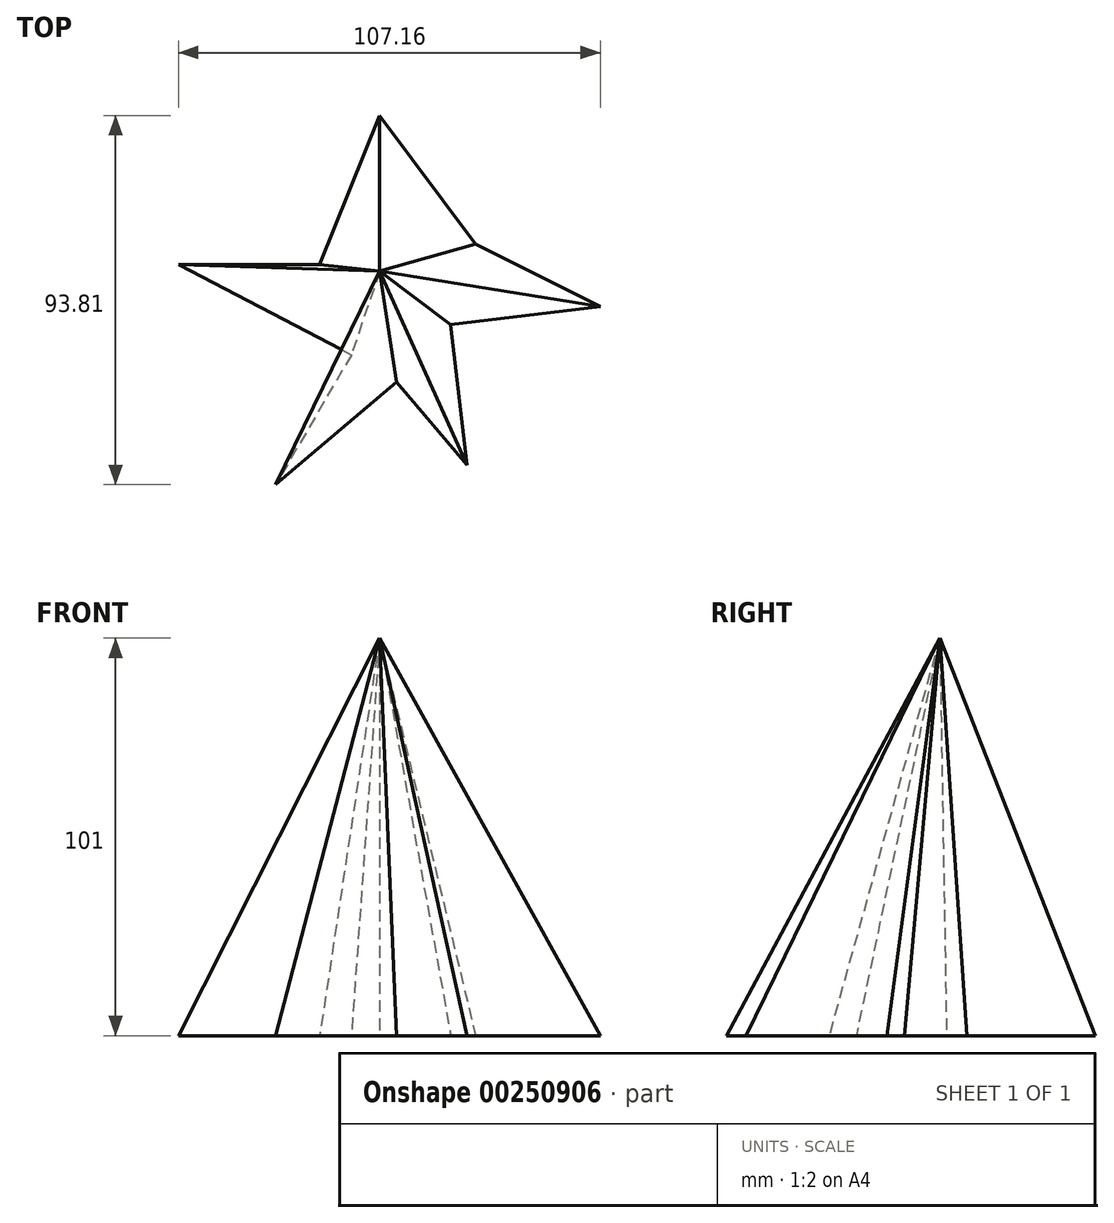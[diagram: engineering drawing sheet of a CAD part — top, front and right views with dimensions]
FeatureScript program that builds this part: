
annotation { "Feature Type Name" : "Feature", "Feature Type Description" : "" }
export const myFeature = defineFeature(function(context is Context, id is Id, definition is map)
    precondition{}
    {
        {
            var Q0;
            Q0=qCreatedBy(makeId("Top.planeOp"),FACE);
            var sketch = newSketch(context, id + "F0", { "sketchPlane" : qUnion([Q0])});
            skLineSegment(sketch, "E0", {"start": v(0, 44.9) * mm, "end": v(-15.2, 7.03) * mm});
            skLineSegment(sketch, "E1", {"start": v(-15.2, 7.03) * mm, "end": v(-51.07, 7.03) * mm});
            skLineSegment(sketch, "E2", {"start": v(-51.07, 7.03) * mm, "end": v(-7.17, -15.92) * mm});
            skLineSegment(sketch, "E3", {"start": v(-7.17, -15.92) * mm, "end": v(-26.4, -48.91) * mm});
            skLineSegment(sketch, "E4", {"start": v(-26.4, -48.91) * mm, "end": v(4.3, -22.8) * mm});
            skLineSegment(sketch, "E5", {"start": v(4.3, -22.8) * mm, "end": v(22.26, -43.92) * mm});
            skLineSegment(sketch, "E6", {"start": v(22.26, -43.92) * mm, "end": v(18.07, -8.18) * mm});
            skLineSegment(sketch, "E7", {"start": v(18.07, -8.18) * mm, "end": v(56.1, -3.72) * mm});
            skLineSegment(sketch, "E8", {"start": v(56.1, -3.72) * mm, "end": v(24.39, 12.2) * mm});
            skLineSegment(sketch, "E9", {"start": v(24.39, 12.2) * mm, "end": v(0, 44.9) * mm});
            skSolve(sketch);
        }
        {
            var Q0;
            Q0=qCreatedBy(makeId("Top.planeOp"),FACE);
            cPlane(context, id + "F1", {"entities" : qUnion([Q0]), "cplaneType" : CPlaneType.OFFSET, "offset" : 101 * mm, "width" : 150 * mm, "height" : 150 * mm});
        }
        {
            var Q0;
            Q0=qCreatedBy(id+"F1.planeOp",FACE);
            var sketch = newSketch(context, id + "F2", { "sketchPlane" : qUnion([Q0])});
            skPoint(sketch, "E10", {"position": v(0, 5.3) * mm});
            skSolve(sketch);
        }
        {
            var Q0;
            Q0=sQuery(id+"F2.wireOp",VERTEX,"E10");
            var Q1;
            Q1=makeQuery(id+"F0.imprint","IMPRINT",FACE,{"disambiguationData":[TD([[makeQuery(id+"F0.imprint","IMPRINT",EDGE,{"derivedFrom":sQuery(id+"F0.wireOp",EDGE,"E0")}),1.0]])]});
            loft(context, id + "F3", {"sheetProfilesArray" : [{ "sheetProfileEntities" : qUnion([Q0]) }, { "sheetProfileEntities" : qUnion([Q1]) }]});
        }
    });
